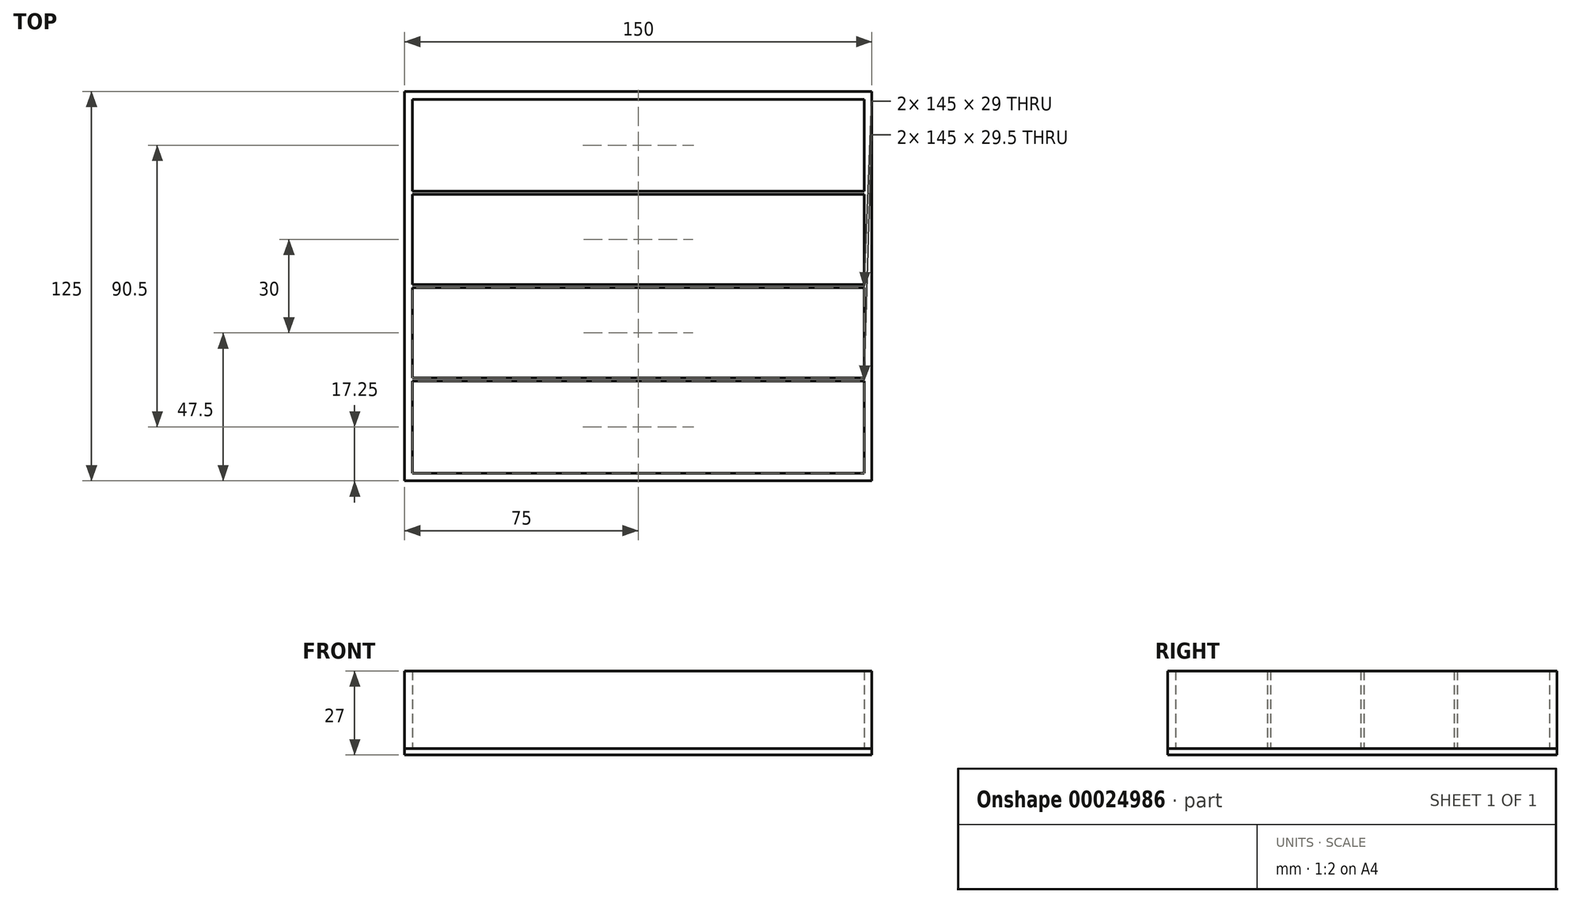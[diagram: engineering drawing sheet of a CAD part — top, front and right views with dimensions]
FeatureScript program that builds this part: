
annotation { "Feature Type Name" : "Feature", "Feature Type Description" : "" }
export const myFeature = defineFeature(function(context is Context, id is Id, definition is map)
    precondition{}
    {
        {
            var Q0;
            Q0=qCreatedBy(makeId("Top.planeOp"),FACE);
            var sketch = newSketch(context, id + "F0", { "sketchPlane" : qUnion([Q0])});
            skLineSegment(sketch, "E0.bottom", {"start": v(-75, 62.5) * mm, "end": v(75, 62.5) * mm});
            skLineSegment(sketch, "E0.top", {"start": v(-75, -62.5) * mm, "end": v(75, -62.5) * mm});
            skLineSegment(sketch, "E0.left", {"start": v(-75, 62.5) * mm, "end": v(-75, -62.5) * mm});
            skLineSegment(sketch, "E0.right", {"start": v(75, 62.5) * mm, "end": v(75, -62.5) * mm});
            skPoint(sketch, "E1", {"position": v(0, 62.5) * mm});
            skPoint(sketch, "E2", {"position": v(-75, 0) * mm});
            skSolve(sketch);
        }
        {
            var Q0;
            Q0=makeQuery(id+"F0.imprint","IMPRINT",FACE,{"disambiguationData":[TD([[makeQuery(id+"F0.imprint","IMPRINT",EDGE,{"derivedFrom":sQuery(id+"F0.wireOp",EDGE,"E0.bottom")}),-1.0]])]});
            extrude(context, id + "F1", {"entities" : qUnion([Q0]), "oppositeDirection" : true, "depth" : 2 * mm});
        }
        {
            var Q0;
            Q0=makeQuery(id+"F0.imprint","IMPRINT",FACE,{"disambiguationData":[TD([[makeQuery(id+"F0.imprint","IMPRINT",EDGE,{"derivedFrom":sQuery(id+"F0.wireOp",EDGE,"E0.bottom")}),-1.0]])]});
            var sketch = newSketch(context, id + "F2", { "sketchPlane" : qUnion([Q0])});
            skLineSegment(sketch, "E3", {"start": v(-75, 62.5) * mm, "end": v(-75, 0) * mm});
            skLineSegment(sketch, "E4", {"start": v(-75, 0) * mm, "end": v(-75, -62.5) * mm});
            skLineSegment(sketch, "E5", {"start": v(-75, -62.5) * mm, "end": v(0, -62.5) * mm});
            skLineSegment(sketch, "E6", {"start": v(0, -62.5) * mm, "end": v(75, -62.5) * mm});
            skLineSegment(sketch, "E7", {"start": v(75, -62.5) * mm, "end": v(75, 0) * mm});
            skLineSegment(sketch, "E8", {"start": v(75, 0) * mm, "end": v(75, 62.5) * mm});
            skLineSegment(sketch, "E9", {"start": v(75, 62.5) * mm, "end": v(0, 62.5) * mm});
            skLineSegment(sketch, "E10", {"start": v(0, 62.5) * mm, "end": v(-75, 62.5) * mm});
            skLineSegment(sketch, "E11.0", {"start": v(72.5, 60) * mm, "end": v(0, 60) * mm});
            skLineSegment(sketch, "E11.1", {"start": v(72.5, 0) * mm, "end": v(72.5, 60) * mm});
            skLineSegment(sketch, "E11.2", {"start": v(72.5, -60) * mm, "end": v(72.5, 0) * mm});
            skLineSegment(sketch, "E11.3", {"start": v(0, -60) * mm, "end": v(72.5, -60) * mm});
            skLineSegment(sketch, "E11.4", {"start": v(-72.5, -60) * mm, "end": v(0, -60) * mm});
            skLineSegment(sketch, "E11.5", {"start": v(0, 60) * mm, "end": v(-72.5, 60) * mm});
            skLineSegment(sketch, "E11.6", {"start": v(-72.5, 0) * mm, "end": v(-72.5, -60) * mm});
            skLineSegment(sketch, "E11.7", {"start": v(-72.5, 60) * mm, "end": v(-72.5, 0) * mm});
            skPoint(sketch, "E12", {"position": v(-72.5, 30) * mm});
            skPoint(sketch, "E13", {"position": v(-72.5, -30) * mm});
            skLineSegment(sketch, "E14.bottom", {"start": v(-72.5, 30.5) * mm, "end": v(72.5, 30.5) * mm});
            skLineSegment(sketch, "E14.top", {"start": v(-72.5, 29.5) * mm, "end": v(72.5, 29.5) * mm});
            skLineSegment(sketch, "E14.left", {"start": v(-72.5, 30.5) * mm, "end": v(-72.5, 29.5) * mm});
            skLineSegment(sketch, "E14.right", {"start": v(72.5, 30.5) * mm, "end": v(72.5, 29.5) * mm});
            skLineSegment(sketch, "E15.bottom", {"start": v(-72.5, 0.5) * mm, "end": v(72.5, 0.5) * mm});
            skLineSegment(sketch, "E15.top", {"start": v(-72.5, -0.5) * mm, "end": v(72.5, -0.5) * mm});
            skLineSegment(sketch, "E15.left", {"start": v(-72.5, 0.5) * mm, "end": v(-72.5, -0.5) * mm});
            skLineSegment(sketch, "E15.right", {"start": v(72.5, 0.5) * mm, "end": v(72.5, -0.5) * mm});
            skLineSegment(sketch, "E16.bottom", {"start": v(-72.5, -29.5) * mm, "end": v(72.5, -29.5) * mm});
            skLineSegment(sketch, "E16.top", {"start": v(-72.5, -30.5) * mm, "end": v(72.5, -30.5) * mm});
            skLineSegment(sketch, "E16.left", {"start": v(-72.5, -29.5) * mm, "end": v(-72.5, -30.5) * mm});
            skLineSegment(sketch, "E16.right", {"start": v(72.5, -29.5) * mm, "end": v(72.5, -30.5) * mm});
            skSolve(sketch);
        }
        {
            var Q0;
            Q0=makeQuery(id+"F2.imprint","IMPRINT",FACE,{"disambiguationData":[TD([[makeQuery(id+"F2.imprint","IMPRINT",EDGE,{"derivedFrom":sQuery(id+"F2.wireOp",EDGE,"E3")}),1.0]])]});
            var Q1;
            Q1=makeQuery(id+"F2.imprint","IMPRINT",FACE,{"disambiguationData":[TD([[makeQuery(id+"F2.imprint","IMPRINT",EDGE,{"derivedFrom":sQuery(id+"F2.wireOp",EDGE,"E14.bottom")}),-1.0]])]});
            var Q2;
            {var subQ3=sQuery(id+"F2.wireOp",EDGE,"E15.bottom");Q2=makeQuery(id+"F2.imprint","IMPRINT",FACE,{"disambiguationData":[TD([[makeQuery(id+"F2.imprint","IMPRINT",EDGE,{"derivedFrom":subQ3}),-1.0]])]});}
            var Q3;
            Q3=makeQuery(id+"F2.imprint","IMPRINT",FACE,{"disambiguationData":[TD([[makeQuery(id+"F2.imprint","IMPRINT",EDGE,{"derivedFrom":sQuery(id+"F2.wireOp",EDGE,"E16.bottom")}),-1.0]])]});
            extrude(context, id + "F3", {"entities" : qUnion([Q0, Q1, Q2, Q3]), "depth" : 25 * mm});
        }
    });
